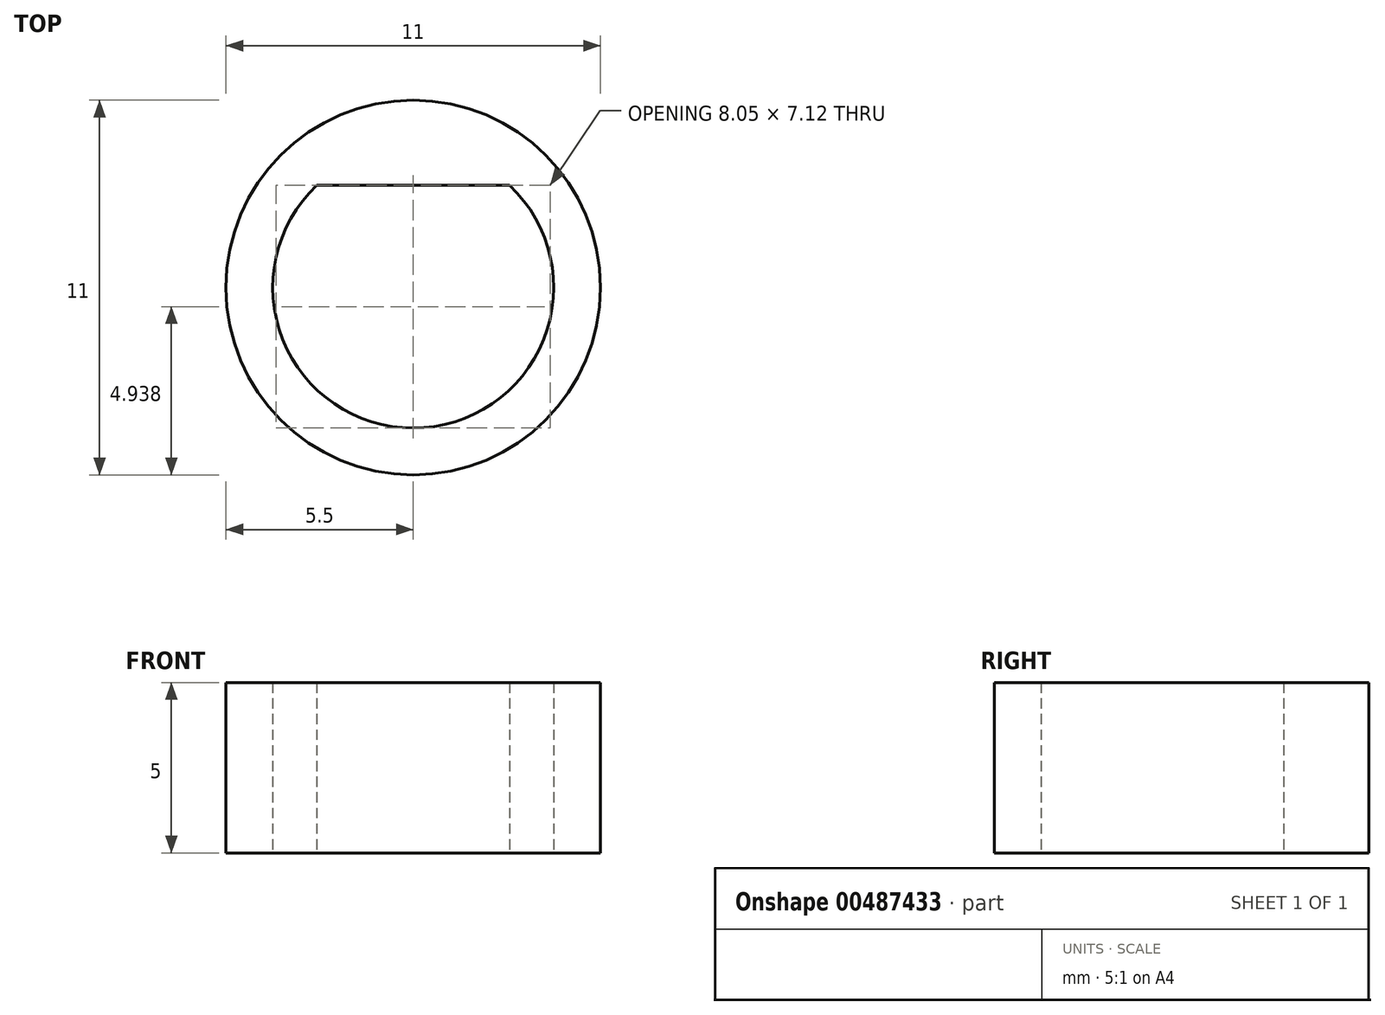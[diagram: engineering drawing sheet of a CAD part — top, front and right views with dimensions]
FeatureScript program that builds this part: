
annotation { "Feature Type Name" : "Feature", "Feature Type Description" : "" }
export const myFeature = defineFeature(function(context is Context, id is Id, definition is map)
    precondition{}
    {
        {
            var Q0;
            Q0=qCreatedBy(makeId("Top.planeOp"),FACE);
            var sketch = newSketch(context, id + "F0", { "sketchPlane" : qUnion([Q0])});
            skLineSegment(sketch, "E0", {"start": v(0, -4) * mm, "end": v(0, 3) * mm});
            skLineSegment(sketch, "E1", {"start": v(0, 3) * mm, "end": v(2.83, 3) * mm});
            skLineSegment(sketch, "E2", {"start": v(0, 3) * mm, "end": v(-2.83, 3) * mm});
            skPoint(sketch, "E3.endSnap0", {"position": v(-5.5, 0) * mm});
            skCircle(sketch, "E4", {"center": v(0, 0) * mm, "radius": 5.5 * mm});
            skArc(sketch, "E5", {"start": v(-2.83, 3) * mm, "mid": v(0, -4.12) * mm, "end": v(2.83, 3) * mm});
            skSolve(sketch);
        }
        {
            var Q0;
            Q0 = qSketchRegion(id + "F0", true);
            extrude(context, id + "F1", {"entities" : qUnion([Q0]), "depth" : 5 * mm});
        }
    });
